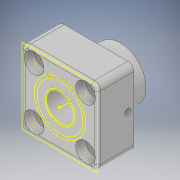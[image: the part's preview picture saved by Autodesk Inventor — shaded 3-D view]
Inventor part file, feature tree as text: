
AUTODESK INVENTOR PART (.ipt)
format: ipt  version: 2019 (Build 230136000, 136)  size: 226,304 bytes
history: native  units: mm
features: other x5, fillet x2, sketch x2
ambient origin geometry x8: Origin, YZ Plane, XZ Plane, XY Plane, X Axis, Y Axis, Z Axis, Center Point
bodies: Volumenkörper1 (feature_tree), Volumenkörper2 (feature_tree), Volumenkörper3 (feature_tree)
feature tree (9):
  other  "Oberteil_Zerstäuber.ipt"
  fillet  "Rundung1"  Radius=10.0mm
  fillet  "Rundung2"  Radius=2.0mm
  other  "Volumenkörper2::Oberteil_Zerstäuber.ipt"
  other  "Volumenkörper3::Oberteil_Zerstäuber.ipt"
  other  "Volumenkörper4::Oberteil_Zerstäuber.ipt"
  other  "Bezeichnung1"
  sketch  "Skizze1"  dims[d2=1.0mm]
  sketch  "Skizze2"
